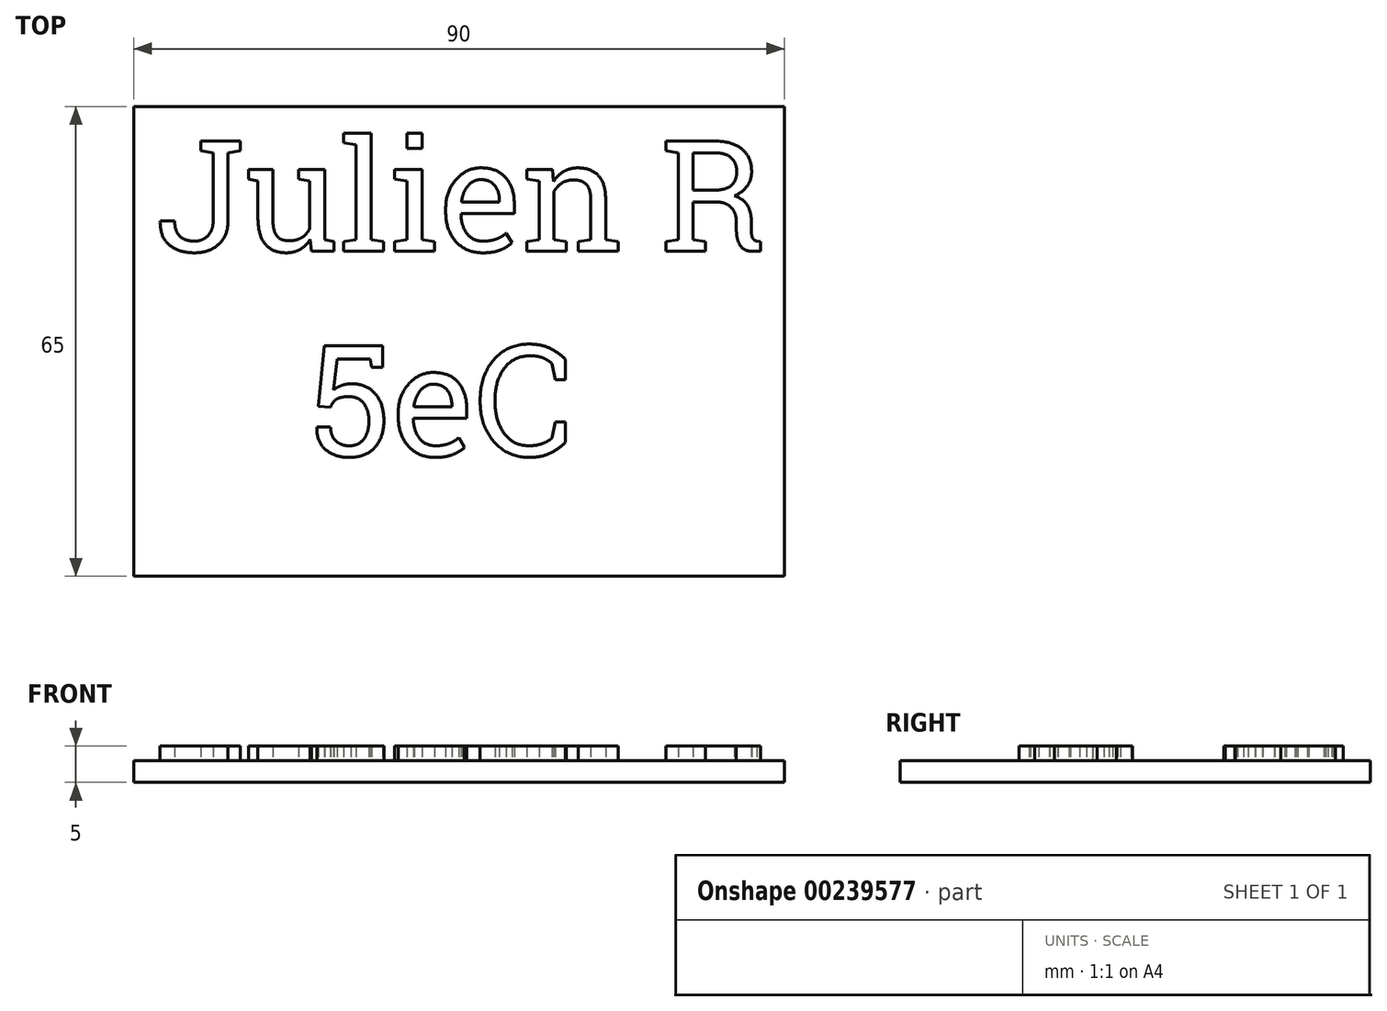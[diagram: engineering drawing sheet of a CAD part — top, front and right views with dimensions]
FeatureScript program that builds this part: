
annotation { "Feature Type Name" : "Feature", "Feature Type Description" : "" }
export const myFeature = defineFeature(function(context is Context, id is Id, definition is map)
    precondition{}
    {
        {
            var Q0;
            Q0=qCreatedBy(makeId("Top.planeOp"),FACE);
            var sketch = newSketch(context, id + "F0", { "sketchPlane" : qUnion([Q0])});
            skLineSegment(sketch, "E0.bottom", {"start": v(0, 0) * mm, "end": v(90, 0) * mm});
            skLineSegment(sketch, "E0.top", {"start": v(0, -65) * mm, "end": v(90, -65) * mm});
            skLineSegment(sketch, "E0.left", {"start": v(0, 0) * mm, "end": v(0, -65) * mm});
            skLineSegment(sketch, "E0.right", {"start": v(90, 0) * mm, "end": v(90, -65) * mm});
            skSolve(sketch);
        }
        {
            var Q0;
            Q0=makeQuery(id+"F0.imprint","IMPRINT",FACE,{"disambiguationData":[TD([[makeQuery(id+"F0.imprint","IMPRINT",EDGE,{"derivedFrom":sQuery(id+"F0.wireOp",EDGE,"E0.bottom")}),-1.0]])]});
            extrude(context, id + "F1", {"entities" : qUnion([Q0]), "depth" : 3 * mm});
        }
        {
            var Q0;
            Q0=makeQuery(id+"F1.opExtrude","CAP_FACE",FACE,{"disambiguationData":[OSD([sQuery(id+"F0.wireOp",EDGE,"E0.bottom"),sQuery(id+"F0.wireOp",EDGE,"E0.top"),sQuery(id+"F0.wireOp",EDGE,"E0.left"),sQuery(id+"F0.wireOp",EDGE,"E0.right")])],"isStart":false});
            var sketch = newSketch(context, id + "F2", { "sketchPlane" : qUnion([Q0])});
            skSolve(sketch);
        }
        {
            var Q0;
            Q0=makeQuery(id+"F2.imprint","IMPRINT",FACE,{"disambiguationData":[TD([[makeQuery(id+"F2.imprint","IMPRINT",EDGE,{"derivedFrom":makeQuery(id+"F1.opExtrude","CAP_EDGE",EDGE,{"disambiguationData":[OSD([sQuery(id+"F0.wireOp",EDGE,"E0.bottom")])],"isStart":false})}),-1.0]])]});
            var sketch = newSketch(context, id + "F3", { "sketchPlane" : qUnion([Q0])});
            skText(sketch, "E1", { "text": "Julien R\n    5eC", "fontName": "RobotoSlab-Regular.ttf"});
            const initialGuessF3  = {"E1": [0.003, -0.02003, 1, 0, 0.01544]};
            skSetInitialGuess(sketch, initialGuessF3);
            skSolve(sketch);
        }
        {
            var Q0;
            Q0=makeQuery(id+"F2.imprint","IMPRINT",FACE,{"disambiguationData":[TD([[makeQuery(id+"F2.imprint","IMPRINT",EDGE,{"derivedFrom":makeQuery(id+"F1.opExtrude","CAP_EDGE",EDGE,{"disambiguationData":[OSD([sQuery(id+"F0.wireOp",EDGE,"E0.bottom")])],"isStart":false})}),-1.0]])]});
            var sketch = newSketch(context, id + "F4", { "sketchPlane" : qUnion([Q0])});
            skSolve(sketch);
        }
        {
            var Q0;
            Q0 = qSketchRegion(id + "F4", true);
            var Q1;
            Q1 = qSketchRegion(id + "F3", true);
            extrude(context, id + "F5", {"entities" : qUnion([Q0, Q1]), "operationType" : NewBodyOperationType.ADD, "depth" : 2 * mm});
        }
    });
